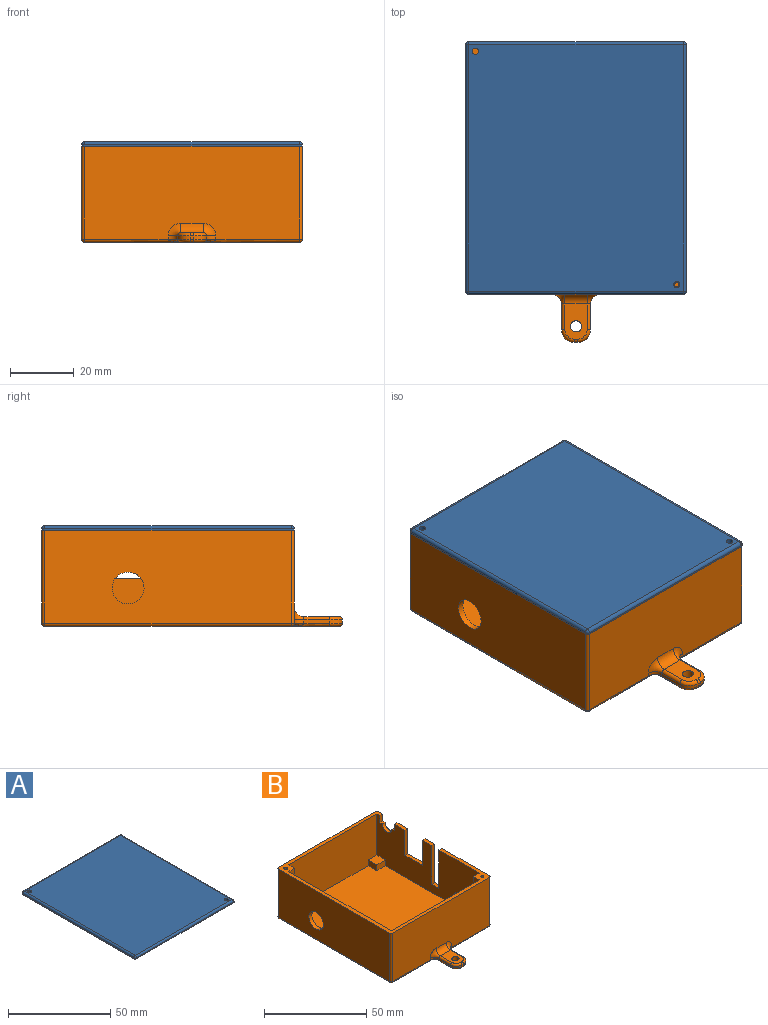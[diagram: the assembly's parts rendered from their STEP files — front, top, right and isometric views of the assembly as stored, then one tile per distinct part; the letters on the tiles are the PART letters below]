
ASSEMBLY  parts=2 mates=1
PART A: 58 faces, bbox 69x79x9 mm
  f0: plane 2.5x1.5mm, normal (0,0,-1), area 3.7mm2, adj f3,f41,f42,f45
  f1: plane 7x2.5mm, normal (0,0,-1), area 17.5mm2, adj f3,f25,f33,f38
  f2: plane 79x69mm, normal (0,0,-1), area 4834.9mm2, adj f3,f4,f5,f6,f7,f8,f10,f11
  f3: plane 77x8mm, normal (1,0,0), area 151.2mm2, adj f0,f1,f2,f33,f35,f36,f38,f39
  f4: plane 67x0.5mm, normal (0,1,0), area 33.5mm2, adj f2,f51,f55,f57
  f5: plane 77x0.5mm, normal (-1,0,0), area 38.5mm2, adj f2,f46,f50,f51
  f6: cylinder r=1mm len=2mm, axis (0,0,-1), area 9.4mm2, adj f2,f9
  f7: plane 67x0.5mm, normal (0,-1,0), area 33.5mm2, adj f2,f46,f48,f49
  f8: cylinder r=1mm len=2mm, axis (0,0,-1), area 9.4mm2, adj f2,f9
  f9: plane 77x67mm, normal (0,0,1), area 5152.7mm2, adj f6,f8,f49,f50,f54,f55
  f10: plane 39x2mm, normal (0,1,0), area 78mm2, adj f2,f11,f13,f14
  f11: plane 4x2mm, normal (-1,0,0), area 8mm2, adj f2,f10,f12,f14
  f12: plane 39x2mm, normal (0,-1,0), area 78mm2, adj f2,f11,f13,f14
  f13: plane 4x2mm, normal (1,0,0), area 8mm2, adj f2,f10,f12,f14
  f14: plane 39x4mm, normal (0,0,-1), area 156mm2, adj f10,f11,f12,f13
  f15: plane 39x2mm, normal (0,1,0), area 78mm2, adj f2,f16,f18,f19
  f16: plane 4x2mm, normal (-1,0,0), area 8mm2, adj f2,f15,f17,f19
  f17: plane 39x2mm, normal (0,-1,0), area 78mm2, adj f2,f16,f18,f19
  f18: plane 4x2mm, normal (1,0,0), area 8mm2, adj f2,f15,f17,f19
  f19: plane 39x4mm, normal (0,0,-1), area 156mm2, adj f15,f16,f17,f18
  f20: plane 4x2mm, normal (0,1,0), area 8mm2, adj f2,f21,f23,f24
  f21: plane 25x2mm, normal (-1,0,0), area 50mm2, adj f2,f20,f22,f24
  f22: plane 4x2mm, normal (0,-1,0), area 8mm2, adj f2,f21,f23,f24
  f23: plane 25x2mm, normal (1,0,0), area 50mm2, adj f2,f20,f22,f24
  f24: plane 25x4mm, normal (0,0,-1), area 100mm2, adj f20,f21,f22,f23
  f25: plane 7x2mm, normal (1,0,0), area 14mm2, adj f1,f28,f33,f38
  f26: plane 4x2mm, normal (0,1,0), area 8mm2, adj f2,f27,f28,f37
  f27: plane 13.25x2mm, normal (-1,0,0), area 26.5mm2, adj f2,f26,f28,f33
  f28: plane 13.25x4mm, normal (0,0,-1), area 53mm2, adj f25,f26,f27,f33,f37
  f29: plane 7.25x2mm, normal (1,0,0), area 14.5mm2, adj f2,f31,f32,f35
  f30: plane 7.25x2mm, normal (-1,0,0), area 14.5mm2, adj f2,f31,f32,f35
  f31: plane 4x2mm, normal (0,-1,0), area 8mm2, adj f2,f29,f30,f32
  f32: plane 7.25x4mm, normal (0,0,-1), area 29mm2, adj f29,f30,f31,f35
  f33: plane 10x7.5mm, normal (0,1,0), area 67mm2, adj f1,f2,f3,f25,f27,f28,f34,f36
  f34: plane 7.5x4.5mm, normal (-1,0,0), area 33.8mm2, adj f2,f33,f35,f36
  f35: plane 10x7.5mm, normal (0,-1,0), area 67mm2, adj f2,f3,f29,f30,f32,f34,f36
  f36: plane 10x4.5mm, normal (0,0,-1), area 45mm2, adj f3,f33,f34,f35
  f37: plane 11.5x5mm, normal (-1,0,0), area 45mm2, adj f2,f26,f28,f38,f39,f40
  f38: plane 5x2.5mm, normal (0,-1,0), area 12.5mm2, adj f1,f3,f25,f37,f40
  f39: plane 5x2.5mm, normal (0,1,0), area 12.5mm2, adj f2,f3,f37,f40
  f40: plane 11.5x2.5mm, normal (0,0,-1), area 28.8mm2, adj f3,f37,f38,f39
  f41: plane 4x2.5mm, normal (0,1,0), area 10mm2, adj f0,f2,f3,f42
  f42: plane 9.5x4mm, normal (-1,0,0), area 21.4mm2, adj f0,f2,f41,f43,f44,f45
  f43: plane 4x2.5mm, normal (0,-1,0), area 10mm2, adj f2,f3,f42,f44
  f44: plane 2.5x1.5mm, normal (0,0,-1), area 3.8mm2, adj f3,f42,f43,f45
  f45: cylinder r=3.25mm len=6.5mm, axis (1,0,0), area 25.5mm2, adj f0,f3,f42,f44
  f46: cylinder r=1mm len=1mm, axis (0,0,1), area 0.8mm2, adj f2,f5,f7,f47
  f47: sphere r=1mm, area 1.6mm2, adj f46,f49,f50
  f48: cylinder r=1mm len=1mm, axis (0,0,-1), area 0.8mm2, adj f2,f3,f7,f52
  f49: cylinder r=1mm len=67mm, axis (-1,0,0), area 105.2mm2, adj f7,f9,f47,f52
  f50: cylinder r=1mm len=77mm, axis (0,1,0), area 121mm2, adj f5,f9,f47,f53
  f51: cylinder r=1mm len=1mm, axis (0,0,-1), area 0.8mm2, adj f2,f4,f5,f53
  f52: sphere r=1mm, area 1.6mm2, adj f48,f49,f54
  f53: sphere r=1mm, area 1.6mm2, adj f50,f51,f55
  f54: cylinder r=1mm len=77mm, axis (0,-1,0), area 121mm2, adj f3,f9,f52,f56
  f55: cylinder r=1mm len=67mm, axis (1,0,0), area 105.2mm2, adj f4,f9,f53,f56
  f56: sphere r=1mm, area 1.6mm2, adj f54,f55,f57
  f57: cylinder r=1mm len=1mm, axis (0,0,1), area 0.8mm2, adj f2,f3,f4,f56
PART B: 91 faces, bbox 69.4x94.8x30.4 mm
  f0: bspline ~3.47x3.47mm, area 4.6mm2, adj f73,f75,f84,f85
  f1: bspline ~3.47x3.47mm, area 4.6mm2, adj f81,f83,f89,f90
  f2: plane 4.42x4.42mm, normal (0.71,0,-0.71), area 17.9mm2, adj f4,f5,f50,f51,f52
  f3: plane 75x28mm, normal (-1,0,0), area 1664.3mm2, adj f4,f6,f7,f9,f14,f15,f16,f17
  f4: plane 65x28mm, normal (0,-1,0), area 1758mm2, adj f2,f3,f5,f6,f9,f24,f25,f27
  f5: plane 75x28mm, normal (1,0,0), area 1951.5mm2, adj f2,f4,f6,f9,f16,f26,f28,f29
  f6: plane 79x69mm, normal (0,0,1), area 520.5mm2, adj f3,f4,f5,f8,f10,f11,f12,f16
  f7: plane 7.5x2mm, normal (0,0,1), area 15mm2, adj f3,f8,f40,f46
  f8: plane 77x29mm, normal (1,0,0), area 1867.3mm2, adj f6,f7,f14,f15,f17,f39,f40,f41
  f9: plane 75x65mm, normal (0,0,1), area 4702.7mm2, adj f3,f4,f5,f16,f23,f24,f26,f27
  f10: plane 67x29mm, normal (0,1,0), area 1943mm2, adj f6,f66,f71,f72
  f11: plane 77x29mm, normal (-1,0,0), area 2154.5mm2, adj f6,f60,f72,f76,f77
  f12: plane 67x29mm, normal (0,-1,0), area 1874.9mm2, adj f6,f67,f73,f77,f81,f85,f86,f87
  f13: plane 92x67mm, normal (0,0,-1), area 5250.5mm2, adj f21,f68,f71,f73,f75,f76,f78,f80
  f14: plane 23x2mm, normal (0,-1,0), area 46mm2, adj f3,f8,f15,f39
  f15: plane 6.5x2mm, normal (0,0,1), area 13mm2, adj f3,f8,f14,f41
  f16: plane 65x28mm, normal (0,1,0), area 1758mm2, adj f3,f5,f6,f9,f30,f31,f33,f34
  f17: plane 23x2mm, normal (0,1,0), area 46mm2, adj f3,f6,f8,f39
  f18: plane 8x1mm, normal (-1,0,0), area 8mm2, adj f58,f65,f83,f89
  f19: plane 1x1mm, normal (0,-1,0), area 1mm2, adj f58,f59,f63,f80
  f20: plane 8x1mm, normal (1,0,0), area 8mm2, adj f59,f61,f75,f85
  f21: cylinder r=1.75mm len=3.5mm, axis (0,0,1), area 33mm2, adj f13,f22
  f22: plane 11x7mm, normal (0,0,1), area 63.5mm2, adj f21,f61,f62,f63,f64,f65,f87
  f23: plane 6x3.5mm, normal (0,-1,0), area 21mm2, adj f3,f9,f24,f25
  f24: plane 6x3.5mm, normal (-1,0,0), area 21mm2, adj f4,f9,f23,f25
  f25: plane 6x6mm, normal (0,0,1), area 36mm2, adj f3,f4,f23,f24
  f26: plane 6x3.5mm, normal (0,-1,0), area 21mm2, adj f5,f9,f27,f28
  f27: plane 6x3.5mm, normal (1,0,0), area 21mm2, adj f4,f9,f26,f28
  f28: plane 6x6mm, normal (0,0,1), area 36mm2, adj f4,f5,f26,f27
  f29: plane 6x3.5mm, normal (0,1,0), area 21mm2, adj f5,f9,f30,f31
  f30: plane 6x3.5mm, normal (1,0,0), area 21mm2, adj f9,f16,f29,f31
  f31: plane 6x6mm, normal (0,0,1), area 36mm2, adj f5,f16,f29,f30
  f32: plane 6x3.5mm, normal (0,1,0), area 21mm2, adj f3,f9,f33,f34
  f33: plane 6x3.5mm, normal (-1,0,0), area 21mm2, adj f9,f16,f32,f34
  f34: plane 6x6mm, normal (0,0,1), area 36mm2, adj f3,f16,f32,f33
  f35: cylinder r=1mm len=3.5mm, axis (0,0,-1), area 22mm2, adj f37,f38
  f36: cylinder r=3mm len=6mm, axis (0,0,-1), area 66mm2, adj f9,f37
  f37: plane 6x6mm, normal (0,0,1), area 25.1mm2, adj f35,f36
  f38: plane 2x2mm, normal (0,0,1), area 3.1mm2, adj f35
  f39: plane 5x2mm, normal (0,0,1), area 10mm2, adj f3,f8,f14,f17
  f40: plane 15x2mm, normal (0,-1,0), area 30mm2, adj f3,f7,f8,f42
  f41: plane 15x2mm, normal (0,1,0), area 30mm2, adj f3,f8,f15,f42
  f42: plane 12x2mm, normal (0,0,1), area 24mm2, adj f3,f8,f40,f41
  f43: cylinder r=3.25mm len=6.5mm, axis (1,0,0), area 20.4mm2, adj f3,f8,f44,f47
  f44: plane 2x1.75mm, normal (0,0,1), area 3.5mm2, adj f3,f8,f43,f45
  f45: plane 4x2mm, normal (0,-1,0), area 8mm2, adj f3,f6,f8,f44
  f46: plane 4x2mm, normal (0,1,0), area 8mm2, adj f3,f7,f8,f47
  f47: plane 2x1.75mm, normal (0,0,1), area 3.5mm2, adj f3,f8,f43,f46
  f48: cylinder r=1.5mm len=3mm, axis (1,0,0), area 18.8mm2, adj f3,f8
  f49: cylinder r=1.5mm len=3mm, axis (1,0,0), area 18.8mm2, adj f3,f8
  f50: cylinder r=1mm len=7mm, axis (0,0,1), area 37.7mm2, adj f2,f6,f56
  f51: plane 7x4mm, normal (0,-1,0), area 20mm2, adj f2,f5,f6,f52
  f52: plane 4x3mm, normal (1,0,0), area 12mm2, adj f2,f4,f6,f51
  f53: plane 7x4mm, normal (0,1,0), area 20mm2, adj f3,f6,f54,f57
  f54: plane 4x3mm, normal (-1,0,0), area 12mm2, adj f6,f16,f53,f57
  f55: cylinder r=0.68mm len=6.68mm, axis (0,0,1), area 25.7mm2, adj f6,f57
  f56: plane 1.42x1.42mm, normal (0.71,0,-0.71), area 0.3mm2, adj f4,f5,f50
  f57: plane 4.29x4.29mm, normal (-0.71,0,-0.71), area 20.6mm2, adj f3,f16,f53,f54,f55
  f58: cylinder r=4mm len=4mm, axis (0,0,-1), area 6.3mm2, adj f18,f19,f64,f82
  f59: cylinder r=4mm len=4mm, axis (0,0,1), area 6.3mm2, adj f19,f20,f62,f78
  f60: cylinder r=5mm len=10mm, axis (1,0,0), area 62.8mm2, adj f5,f11
  f61: cylinder r=1mm len=8mm, axis (0,1,0), area 12.6mm2, adj f20,f22,f62,f86
  f62: torus R=3mm, axis (0,0,1), area 9mm2, adj f22,f59,f61,f63
  f63: cylinder r=1mm len=1mm, axis (1,0,0), area 1.6mm2, adj f19,f22,f62,f64
  f64: torus R=3mm, axis (0,0,1), area 9mm2, adj f22,f58,f63,f65
  f65: cylinder r=1mm len=8mm, axis (0,-1,0), area 12.6mm2, adj f18,f22,f64,f88
  f66: cylinder r=1mm len=29mm, axis (0,0,1), area 45.6mm2, adj f6,f8,f10,f69
  f67: cylinder r=1mm len=29mm, axis (0,0,-1), area 45.6mm2, adj f6,f8,f12,f70
  f68: cylinder r=1mm len=77mm, axis (0,-1,0), area 121mm2, adj f8,f13,f69,f70
  f69: sphere r=1mm, area 1.6mm2, adj f66,f68,f71
  f70: sphere r=1mm, area 1.6mm2, adj f67,f68,f73
  f71: cylinder r=1mm len=67mm, axis (1,0,0), area 105.2mm2, adj f10,f13,f69,f74
  f72: cylinder r=1mm len=29mm, axis (0,0,-1), area 45.6mm2, adj f6,f10,f11,f74
  f73: cylinder r=1mm len=30mm, axis (-1,0,0), area 43.4mm2, adj f0,f12,f13,f70,f84
  f74: sphere r=1mm, area 1.6mm2, adj f71,f72,f76
  f75: cylinder r=1mm len=12mm, axis (0,-1,0), area 15.2mm2, adj f0,f13,f20,f78,f84
  f76: cylinder r=1mm len=77mm, axis (0,1,0), area 121mm2, adj f11,f13,f74,f79
  f77: cylinder r=1mm len=29mm, axis (0,0,1), area 45.6mm2, adj f6,f11,f12,f79
  f78: torus R=3mm, axis (0,0,1), area 9mm2, adj f13,f59,f75,f80
  f79: sphere r=1mm, area 1.6mm2, adj f76,f77,f81
  f80: cylinder r=1mm len=1mm, axis (-1,0,0), area 1.6mm2, adj f13,f19,f78,f82
  f81: cylinder r=1mm len=30mm, axis (-1,0,0), area 43.4mm2, adj f1,f12,f13,f79,f90
  f82: torus R=3mm, axis (0,0,1), area 9mm2, adj f13,f58,f80,f83
  f83: cylinder r=1mm len=12mm, axis (0,1,0), area 15.2mm2, adj f1,f13,f18,f82,f90
  f84: bspline ~2.14x2.13mm, area 2.1mm2, adj f0,f73,f75
  f85: cylinder r=3mm len=3mm, axis (0,0,1), area 4.7mm2, adj f0,f12,f20,f86
  f86: torus R=4mm, axis (0,-1,0), area 15.5mm2, adj f12,f61,f85,f87
  f87: cylinder r=3mm len=7mm, axis (-1,0,0), area 33mm2, adj f12,f22,f86,f88
  f88: torus R=4mm, axis (0,-1,0), area 15.5mm2, adj f12,f65,f87,f89
  f89: cylinder r=3mm len=3mm, axis (0,0,-1), area 4.7mm2, adj f1,f12,f18,f88
  f90: bspline ~2.34x2.34mm, area 1.4mm2, adj f1,f81,f83
PLACE A t=(0,0,28)mm
PLACE B at identity
MATE fastened A.f2 <-> B.f6  axis (0,0,-1) through (-34.5,0,28)mm
